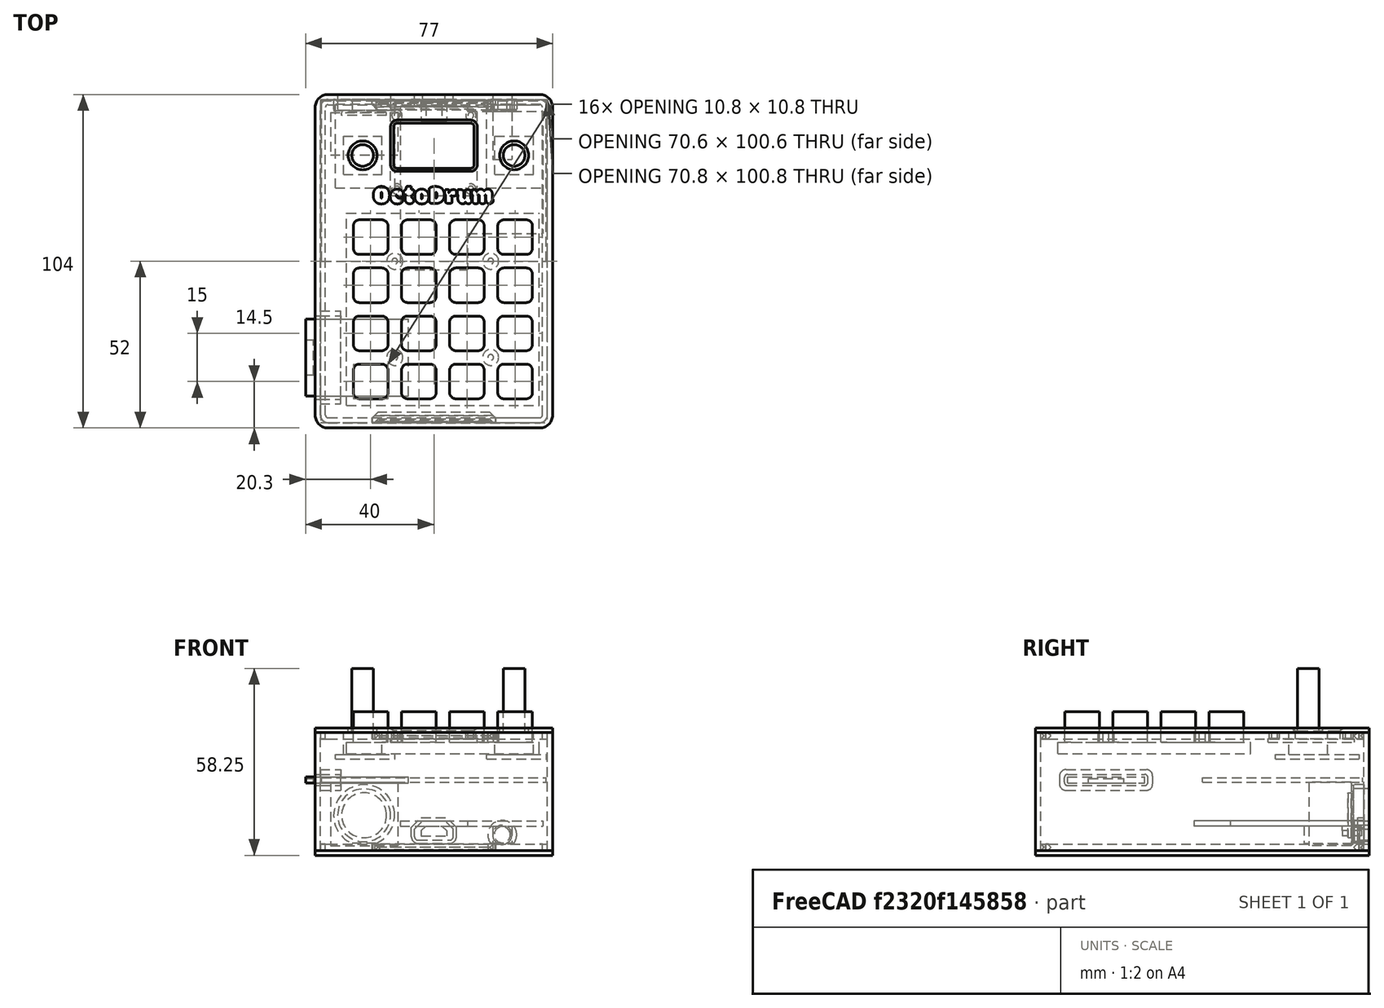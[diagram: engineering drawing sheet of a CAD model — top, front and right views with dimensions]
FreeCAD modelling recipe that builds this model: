
FCSTD DOCUMENT  (FreeCAD 0.19R14555 (Git shallow))
Label: rpi-pico-drum
License: All rights reserved
LicenseURL: http://en.wikipedia.org/wiki/All_rights_reserved
objects: Part::Box×36, Part::MultiFuse×26, Part::Fillet×24, Part::Cut×16, Part::FeaturePython×10, Part::Cylinder×9, Part::Chamfer×8, Part::MultiCommon×4, Mesh::Feature×2, Part::Part2DObjectPython×2, Part::Extrusion×2, Part::Feature×1
note: 138 computed .brp shape members not serialized (recipe doc carries the construction recipe); baked Part::Feature solids carry a one-line shape summary decoded from their .brp

FEATURE [Mesh::Feature] nt_top  label="nt-top"
  Placement = pos=(0,0,5) rot=(1,0,0;3.14159rad)
FEATURE [Part::Box] Box  label="BareFrontPlate"
  AttacherType = Attacher::AttachEngine3D
  Height = 1.5
  Length = 74
  Placement = pos=(-37,-37,3.5) rot=(0,0,1;0rad)
  Width = 104
FEATURE [Part::Box] Box001  label="NeoTrellisPCB"
  AttacherType = Attacher::AttachEngine3D
  Height = 1.5
  Length = 60
  Placement = pos=(-27.2,-30,0) rot=(0,0,1;0rad)
  Width = 60
FEATURE [Part::Box] Box002  label="Cube001"
  AttacherType = Attacher::AttachEngine3D
  Height = 9.5
  Length = 10.8
  Placement = pos=(2.1,2.1,0) rot=(0,0,1;0rad)
  Width = 10.8
FEATURE [Part::Fillet] Fillet  label="NeoTrellisButton"
  Base = -> Box002
  Edges = 4 edges r=1.9: [Edge1,Edge3,Edge5,Edge7]
  Placement = pos=(-30,0,0) rot=(0,0,1;0rad)
FEATURE [Part::Fillet] Fillet001  label="NeoTrellisButton001"
  Base = -> Box002
  Edges = 4 edges r=1.9: [Edge1,Edge3,Edge5,Edge7]
  Placement = pos=(-15,0,0) rot=(0,0,1;0rad)
FEATURE [Part::Fillet] Fillet002  label="NeoTrellisButton002"
  Base = -> Box002
  Edges = 4 edges r=1.9: [Edge1,Edge3,Edge5,Edge7]
FEATURE [Part::Fillet] Fillet003  label="NeoTrellisButton003"
  Base = -> Box002
  Edges = 4 edges r=1.9: [Edge1,Edge3,Edge5,Edge7]
  Placement = pos=(15,0,0) rot=(0,0,1;0rad)
FEATURE [Part::Fillet] Fillet004  label="NeoTrellisButton004"
  Base = -> Box002
  Edges = 4 edges r=1.9: [Edge1,Edge3,Edge5,Edge7]
  Placement = pos=(-30,15,0) rot=(0,0,1;0rad)
FEATURE [Part::Fillet] Fillet005  label="NeoTrellisButton005"
  Base = -> Box002
  Edges = 4 edges r=1.9: [Edge1,Edge3,Edge5,Edge7]
  Placement = pos=(15,15,0) rot=(0,0,1;0rad)
FEATURE [Part::Fillet] Fillet006  label="NeoTrellisButton006"
  Base = -> Box002
  Edges = 4 edges r=1.9: [Edge1,Edge3,Edge5,Edge7]
  Placement = pos=(-15,15,0) rot=(0,0,1;0rad)
FEATURE [Part::Fillet] Fillet007  label="NeoTrellisButton007"
  Base = -> Box002
  Edges = 4 edges r=1.9: [Edge1,Edge3,Edge5,Edge7]
  Placement = pos=(0,15,0) rot=(0,0,1;0rad)
FEATURE [Part::Fillet] Fillet008  label="NeoTrellisButton008"
  Base = -> Box002
  Edges = 4 edges r=1.9: [Edge1,Edge3,Edge5,Edge7]
  Placement = pos=(-30,-15,0) rot=(0,0,1;0rad)
FEATURE [Part::Fillet] Fillet009  label="NeoTrellisButton009"
  Base = -> Box002
  Edges = 4 edges r=1.9: [Edge1,Edge3,Edge5,Edge7]
  Placement = pos=(15,-15,0) rot=(0,0,1;0rad)
FEATURE [Part::Fillet] Fillet010  label="NeoTrellisButton010"
  Base = -> Box002
  Edges = 4 edges r=1.9: [Edge1,Edge3,Edge5,Edge7]
  Placement = pos=(-15,-15,0) rot=(0,0,1;0rad)
FEATURE [Part::Fillet] Fillet011  label="NeoTrellisButton011"
  Base = -> Box002
  Edges = 4 edges r=1.9: [Edge1,Edge3,Edge5,Edge7]
  Placement = pos=(0,-15,0) rot=(0,0,1;0rad)
FEATURE [Part::Fillet] Fillet012  label="NeoTrellisButton012"
  Base = -> Box002
  Edges = 4 edges r=1.9: [Edge1,Edge3,Edge5,Edge7]
  Placement = pos=(-30,-30,0) rot=(0,0,1;0rad)
FEATURE [Part::Fillet] Fillet013  label="NeoTrellisButton013"
  Base = -> Box002
  Edges = 4 edges r=1.9: [Edge1,Edge3,Edge5,Edge7]
  Placement = pos=(15,-30,0) rot=(0,0,1;0rad)
FEATURE [Part::Fillet] Fillet014  label="NeoTrellisButton014"
  Base = -> Box002
  Edges = 4 edges r=1.9: [Edge1,Edge3,Edge5,Edge7]
  Placement = pos=(-15,-30,0) rot=(0,0,1;0rad)
FEATURE [Part::Fillet] Fillet015  label="NeoTrellisButton015"
  Base = -> Box002
  Edges = 4 edges r=1.9: [Edge1,Edge3,Edge5,Edge7]
  Placement = pos=(0,-30,0) rot=(0,0,1;0rad)
FEATURE [Part::Box] Box003  label="BackbonePCB"
  AttacherType = Attacher::AttachEngine3D
  Height = 1.5
  Length = 70
  Placement = pos=(-35,15,-12) rot=(0,0,1;0rad)
  Width = 50
FEATURE [Part::Box] Box004  label="NeoTrellisButtonBase"
  AttacherType = Attacher::AttachEngine3D
  Height = 2
  Length = 60
  Placement = pos=(-30,-30,-2) rot=(0,0,1;0rad)
  Width = 60
FEATURE [Part::MultiFuse] Fusion  label="NeoTrellisButtons"
  Placement = pos=(2.8,0,3.5) rot=(0,0,1;0rad)
  Shapes = -> [Fillet,Fillet012,Fillet014,Fillet015,Fillet013,Fillet011,Fillet003,Fillet001,Fillet002,Fillet005,Fillet007,Fillet008,Fillet006,Fillet004,Fillet009,Fillet010,Box004]
FEATURE [Part::Box] Box005  label="DisplayPCB"
  AttacherType = Attacher::AttachEngine3D
  Height = 1.2
  Length = 27
  Placement = pos=(-13.5,35.5,0) rot=(0,0,1;0rad)
  Width = 27
FEATURE [Part::Box] Box008  label="Cube002"
  AttacherType = Attacher::AttachEngine3D
  Height = 6.75
  Length = 12
  Placement = pos=(-6,-6,1.5) rot=(0,0,1;0rad)
  Width = 12
FEATURE [Part::Cylinder] Cylinder
  Angle = 360
  AttacherType = Attacher::AttachEngine3D
  Height = 20
  Placement = pos=(0,0,8.25) rot=(0,0,1;0rad)
  Radius = 3.375
FEATURE [Part::Box] Box009  label="EncoderPCB003"
  AttacherType = Attacher::AttachEngine3D
  Height = 1.5
  Length = 18.63
  Placement = pos=(-8.5,-10.2,0) rot=(0,0,1;0rad)
  Width = 26.2
FEATURE [Part::MultiFuse] Fusion001  label="MenuEncoder"
  Placement = pos=(25,48,-4.75) rot=(0,0,1;0rad)
  Shapes = -> [Box008,Cylinder,Box009]
FEATURE [Part::MultiFuse] Fusion002  label="ModEncoder"
  Placement = pos=(-22.2,48,-4.75) rot=(0,0,1;0rad)
  Shapes = -> [Box008,Cylinder,Box009]
FEATURE [Part::MultiFuse] Fusion003  label="NeoTrellis"
  Placement = pos=(0,0,-3) rot=(0,0,1;0rad)
  Shapes = -> [Fusion,Box001]
FEATURE [Part::Box] Box010  label="Cube"
  AttacherType = Attacher::AttachEngine3D
  Height = 19.75
  Length = 21
  Placement = pos=(-10.5,0,0) rot=(0,0,1;0rad)
  Width = 13.25
FEATURE [Part::Cylinder] Cylinder001
  Angle = 360
  AttacherType = Attacher::AttachEngine3D
  Height = 1
  Placement = pos=(0,1,10.25) rot=(1,0,0;1.5708rad)
  Radius = 7
FEATURE [Part::Cut] Cut  label="MidiInput"
  Base = -> Box010
  Placement = pos=(-21.75,61.4,-12) rot=(1,0,0;3.14159rad)
  Tool = -> Cylinder001
FEATURE [Part::Box] Box011  label="PicoPCB"
  AttacherType = Attacher::AttachEngine3D
  Height = 1.6
  Length = 21
  Placement = pos=(-10.5,-25.5,0) rot=(0,0,1;0rad)
  Width = 51
FEATURE [Part::Box] Box012  label="Cube003"
  AttacherType = Attacher::AttachEngine3D
  Height = 3.1
  Length = 8
  Placement = pos=(-4,-26.8,1.6) rot=(0,0,1;0rad)
  Width = 6
FEATURE [Part::Chamfer] Chamfer  label="PicoUSB"
  Base = -> Box012
  Edges = 2 edges r=1.5: [Edge4,Edge8]
FEATURE [Part::MultiFuse] Fusion004  label="Pico"
  Placement = pos=(0,37.83,-24) rot=(1,0,0;3.14159rad)
  Shapes = -> [Chamfer,Box011]
FEATURE [Part::Box] Box013  label="I2SPCB"
  AttacherType = Attacher::AttachEngine3D
  Height = 1.6
  Length = 25.4
  Placement = pos=(-12.7,-19.05,0) rot=(0,0,1;0rad)
  Width = 38.1
FEATURE [Part::Box] Box014  label="Cube005"
  AttacherType = Attacher::AttachEngine3D
  Height = 5.5
  Length = 6
  Placement = pos=(-3,0,0) rot=(0,0,1;0rad)
  Width = 15
FEATURE [Part::Cylinder] Cylinder002
  Angle = 360
  AttacherType = Attacher::AttachEngine3D
  Height = 2.25
  Placement = pos=(0,0,2.75) rot=(1,0,0;1.5708rad)
  Radius = 2.5
FEATURE [Part::MultiFuse] Fusion005  label="AudioJack"
  Placement = pos=(0,-19,1.6) rot=(0,0,1;0rad)
  Shapes = -> [Cylinder002,Box014]
FEATURE [Part::MultiFuse] Fusion006  label="UDA1334A"
  Placement = pos=(21.3,42.7,-24) rot=(1,0,0;3.14159rad)
  Shapes = -> [Fusion005,Box013]
FEATURE [Part::Box] Box015  label="SDCard"
  AttacherType = Attacher::AttachEngine3D
  Height = 2
  Length = 32
  Placement = pos=(-16,-12,0) rot=(0,0,1;0rad)
  Width = 24
FEATURE [Part::Box] Box016  label="DisplayVisible"
  AttacherType = Attacher::AttachEngine3D
  Height = 1.8
  Length = 25
  Placement = pos=(-12.5,44,1.2) rot=(0,0,1;0rad)
  Width = 14
FEATURE [Part::MultiFuse] Fusion007  label="Display"
  Placement = pos=(0,0,0.5) rot=(0,0,1;0rad)
  Shapes = -> [Box005,Box016]
FEATURE [Part::Box] Box017  label="uSDCardSlot"
  AttacherType = Attacher::AttachEngine3D
  Height = 1.5
  Length = 2.5
  Placement = pos=(-16,-5.5,0) rot=(0,0,1;0rad)
  Width = 11
FEATURE [Part::Cut] Cut001  label="SDAdapter"
  Base = -> Box015
  Placement = pos=(-24,-15,-12.25) rot=(0,0,1;0rad)
  Tool = -> Box017
FEATURE [Part::MultiFuse] Fusion008  label="Internals"
  Shapes = -> [Box003,Cut,Cut001,Fusion003,Fusion007,Fusion001,Fusion004,Fusion006,Fusion002]
FEATURE [Part::MultiFuse] Fusion009  label="NeoTrellisButtons001"
  Placement = pos=(2.8,0,2.5) rot=(0,0,1;0rad)
  Shapes = -> [Fillet,Fillet012,Fillet014,Fillet015,Fillet013,Fillet011,Fillet003,Fillet001,Fillet002,Fillet005,Fillet007,Fillet008,Fillet006,Fillet004,Fillet009,Fillet010,Box004]
FEATURE [Part::Cylinder] Cylinder003
  Angle = 360
  AttacherType = Attacher::AttachEngine3D
  Height = 1.5
  Placement = pos=(-22.2,48,3.5) rot=(0,0,1;0rad)
  Radius = 4.5
FEATURE [Part::Cylinder] Cylinder004
  Angle = 360
  AttacherType = Attacher::AttachEngine3D
  Height = 1.5
  Placement = pos=(25,48,3.5) rot=(0,0,1;0rad)
  Radius = 4.5
FEATURE [Part::Box] Box018  label="Cube006"
  AttacherType = Attacher::AttachEngine3D
  Height = 1.5
  Length = 25
  Placement = pos=(-12.5,44,3.5) rot=(0,0,1;0rad)
  Width = 14
FEATURE [Part::MultiFuse] Fusion010  label="FrontPlateCutouts"
  Shapes = -> [Fusion009,Cylinder003,Cylinder004,Box018]
FEATURE [Part::Cut] Cut002
  Base = -> Box
  Tool = -> Fusion010
FEATURE [Part::Fillet] Fillet016
  Base = -> Cut002
  Edges = 8 edges: [Edge1 r=4,Edge3 r=4,Edge6 r=4,Edge145 r=4,Edge410 r=1,Edge411 r=1,Edge412 r=1,Edge413 r=1]
FEATURE [Part::Chamfer] Chamfer001
  Base = -> Fillet016
  Edges = 8 edges r=1: [Edge142,Edge143,Edge144,Edge145,Edge146,Edge147,Edge148,Edge149]
FEATURE [Part::Box] Box019  label="Cube007"
  AttacherType = Attacher::AttachEngine3D
  Height = 2
  Length = 1.5
  Placement = pos=(-35.3,-33,1.5) rot=(0,0,1;0rad)
  Width = 96
FEATURE [Part::Cylinder] Cylinder006
  Angle = 90
  AttacherType = Attacher::AttachEngine3D
  Height = 2
  Placement = pos=(33,33,1.5) rot=(0,0,1;0rad)
  Radius = 2.3
FEATURE [Part::Cylinder] Cylinder007
  Angle = 90
  AttacherType = Attacher::AttachEngine3D
  Height = 2
  Placement = pos=(33,33,1.5) rot=(0,0,1;0rad)
  Radius = 0.8
FEATURE [Part::Cut] Cut003  label="Corner"
  Base = -> Cylinder006
  Placement = pos=(0,30,0) rot=(0,0,1;0rad)
  Tool = -> Cylinder007
FEATURE [Part::Cut] Cut004  label="Corner001"
  Base = -> Cylinder006
  Placement = pos=(0,30,0) rot=(0,0,1;1.5708rad)
  Tool = -> Cylinder007
FEATURE [Part::Cut] Cut005  label="Corner002"
  Base = -> Cylinder006
  Placement = pos=(0,0,0) rot=(0,0,-1;1.5708rad)
  Tool = -> Cylinder007
FEATURE [Part::Cut] Cut006  label="Corner003"
  Base = -> Cylinder006
  Placement = pos=(0,0,0) rot=(0,0,1;3.14159rad)
  Tool = -> Cylinder007
FEATURE [Part::Box] Box020  label="Cube008"
  AttacherType = Attacher::AttachEngine3D
  Height = 2
  Length = 1.5
  Placement = pos=(33.8,-33,1.5) rot=(0,0,1;0rad)
  Width = 96
FEATURE [Part::Box] Box021  label="Cube009"
  AttacherType = Attacher::AttachEngine3D
  Height = 2
  Length = 66
  Placement = pos=(-33,-35.3,1.5) rot=(0,0,1;0rad)
  Width = 1.5
FEATURE [Part::Box] Box022  label="Cube010"
  AttacherType = Attacher::AttachEngine3D
  Height = 2
  Length = 66
  Placement = pos=(-33,63.8,1.5) rot=(0,0,1;0rad)
  Width = 1.5
FEATURE [Part::MultiFuse] Fusion011  label="FrontPlateFrame"
  Shapes = -> [Box022,Box020,Box021,Cut003,Cut004,Cut005,Cut006,Box019]
FEATURE [Part::MultiFuse] Fusion012  label="FrontPlate"
  Shapes = -> [Fusion011,Chamfer001]
FEATURE [Part::Box] Box023  label="BareBackPlate"
  AttacherType = Attacher::AttachEngine3D
  Height = 1.5
  Length = 74
  Placement = pos=(-37,-37,-34.75) rot=(0,0,1;0rad)
  Width = 104
FEATURE [Part::Fillet] Fillet017
  Base = -> Box023
  Edges = 4 edges r=4: [Edge1,Edge3,Edge5,Edge7]
FEATURE [Part::MultiFuse] Fusion013  label="FrontPlateFrame001"
  Placement = pos=(0,0,-34.75) rot=(0,0,1;0rad)
  Shapes = -> [Box022,Box020,Box021,Cut003,Cut004,Cut005,Cut006,Box019]
FEATURE [Part::MultiFuse] Fusion014  label="BottomPlate"
  Shapes = -> [Fillet017,Fusion013]
FEATURE [Part::FeaturePython] Tube  # WARN: FeaturePython — macro-defined, semantics opaque (R4)
  AttacherType = Attacher::AttachEngine3D
  Height = 3
  InnerRadius = 0.9
  OuterRadius = 2.5
  Placement = pos=(-12.2,-15,0.5) rot=(0,0,1;0rad)
FEATURE [Part::FeaturePython] Tube001  # WARN: FeaturePython — macro-defined, semantics opaque (R4)
  AttacherType = Attacher::AttachEngine3D
  Height = 3
  InnerRadius = 0.9
  OuterRadius = 2.5
  Placement = pos=(17.7,-15,0.5) rot=(0,0,1;0rad)
FEATURE [Part::FeaturePython] Tube002  # WARN: FeaturePython — macro-defined, semantics opaque (R4)
  AttacherType = Attacher::AttachEngine3D
  Height = 3
  InnerRadius = 0.9
  OuterRadius = 2.5
  Placement = pos=(-12.2,15,0.5) rot=(0,0,1;0rad)
FEATURE [Part::FeaturePython] Tube003  # WARN: FeaturePython — macro-defined, semantics opaque (R4)
  AttacherType = Attacher::AttachEngine3D
  Height = 3
  InnerRadius = 0.9
  OuterRadius = 2.5
  Placement = pos=(17.7,15,0.5) rot=(0,0,1;0rad)
FEATURE [Part::FeaturePython] Tube004  # WARN: FeaturePython — macro-defined, semantics opaque (R4)
  AttacherType = Attacher::AttachEngine3D
  Height = 1.8
  InnerRadius = 0.9
  OuterRadius = 1.6
  Placement = pos=(-11.5,60.5,1.7) rot=(0,0,1;0rad)
FEATURE [Part::FeaturePython] Tube005  # WARN: FeaturePython — macro-defined, semantics opaque (R4)
  AttacherType = Attacher::AttachEngine3D
  Height = 1.8
  InnerRadius = 0.9
  OuterRadius = 1.6
  Placement = pos=(11.5,60.5,1.7) rot=(0,0,1;0rad)
FEATURE [Part::FeaturePython] Tube006  # WARN: FeaturePython — macro-defined, semantics opaque (R4)
  AttacherType = Attacher::AttachEngine3D
  Height = 1.8
  InnerRadius = 0.9
  OuterRadius = 1.6
  Placement = pos=(-11.5,37.5,1.7) rot=(0,0,1;0rad)
FEATURE [Part::FeaturePython] Tube007  # WARN: FeaturePython — macro-defined, semantics opaque (R4)
  AttacherType = Attacher::AttachEngine3D
  Height = 1.8
  InnerRadius = 0.9
  OuterRadius = 1.6
  Placement = pos=(11.5,37.5,1.7) rot=(0,0,1;0rad)
FEATURE [Part::MultiFuse] Fusion015  label="NeoTrellisMounts"
  Shapes = -> [Tube,Tube001,Tube002,Tube003]
FEATURE [Part::MultiFuse] Fusion016  label="DisplayMounts"
  Shapes = -> [Tube004,Tube005,Tube006,Tube007]
FEATURE [Part::MultiFuse] Fusion017
  Shapes = -> [Fusion016,Fusion015,Fusion012]
FEATURE [Part::Part2DObjectPython] ShapeString001  # Draft 2D object (typed FeaturePython)
  FontFile = <userpath>/repos/dcdalrymple/tools/octodrum/assets/Modak-Regular.ttf
  Placement = pos=(-19,33,4.8) rot=(0,0,1;0rad)
  Size = 8
  String = OctoDr
  Tracking = 0
FEATURE [Part::Part2DObjectPython] ShapeString002  # Draft 2D object (typed FeaturePython)
  FontFile = <userpath>/repos/dcdalrymple/tools/octodrum/assets/Modak-Regular.ttf
  Placement = pos=(7.3,33,4.8) rot=(0,0,1;0rad)
  Size = 8
  String = um
  Tracking = 0
FEATURE [Part::Extrusion] Extrude
  Base = -> ShapeString001
  Dir = (0,0,1)
  DirMode = 0
  FaceMakerClass = Part::FaceMakerBullseye
  LengthFwd = 0.4
  LengthRev = 0
  Solid = false
  Symmetric = false
FEATURE [Part::Extrusion] Extrude001
  Base = -> ShapeString002
  Dir = (0,0,1)
  DirMode = 0
  FaceMakerClass = Part::FaceMakerBullseye
  LengthFwd = 0.4
  LengthRev = 0
  Solid = false
  Symmetric = false
FEATURE [Part::MultiFuse] Fusion018  label="Logo"
  Shapes = -> [Extrude,Extrude001]
FEATURE [Part::Cut] Cut007  label="FinalTopPlate"
  Base = -> Fusion017
  Tool = -> Fusion018
FEATURE [Part::Box] Box024  label="Cube011"
  AttacherType = Attacher::AttachEngine3D
  Height = 2
  Length = 38.5
  Placement = pos=(-19.25,-35.3,1.49) rot=(0,0,1;0rad)
  Width = 3.25
FEATURE [Part::Feature] nt_top001_solid  label="nt_top001 (Solid)"
  shape: bbox 74 x 74 x 3.5 mm, 2332 faces (baked)
FEATURE [Part::MultiCommon] Common  label="Snap"
  Placement = pos=(0,0,-34.75) rot=(0,0,1;0rad)
  Shapes = -> [nt_top001_solid,Box024]
FEATURE [Part::Box] Box025  label="Cube012"
  AttacherType = Attacher::AttachEngine3D
  Height = 2
  Length = 38.5
  Placement = pos=(-19.25,-35.3,-33.24) rot=(0,0,1;0rad)
  Width = 100.6
FEATURE [Part::MultiCommon] Common001  label="Snap001"
  Placement = pos=(0,30,-34.75) rot=(0,0,1;3.14159rad)
  Shapes = -> [nt_top001_solid,Box024]
FEATURE [Part::MultiCommon] Common002  label="Snap002"
  Placement = pos=(0,30,0) rot=(0,0,1;3.14159rad)
  Shapes = -> [nt_top001_solid,Box024]
FEATURE [Part::MultiCommon] Common003  label="Snap003"
  Shapes = -> [nt_top001_solid,Box024]
FEATURE [Part::Cut] Cut008
  Base = -> Fusion014
  Tool = -> Box025
FEATURE [Part::MultiFuse] Fusion019  label="BottomPlateSnap"
  Shapes = -> [Common,Common001,Cut008]
FEATURE [Part::Box] Box026  label="Cube013"
  AttacherType = Attacher::AttachEngine3D
  Height = 2
  Length = 38.5
  Placement = pos=(-19.25,-35.3,1.49) rot=(0,0,1;0rad)
  Width = 1.5
FEATURE [Part::Box] Box027  label="Cube014"
  AttacherType = Attacher::AttachEngine3D
  Height = 2
  Length = 38.5
  Placement = pos=(-19.25,63.8,1.49) rot=(0,0,1;0rad)
  Width = 1.5
FEATURE [Part::MultiFuse] Fusion020
  Shapes = -> [Box026,Box027]
FEATURE [Part::Cut] Cut009
  Base = -> Cut007
  Tool = -> Fusion020
FEATURE [Part::MultiFuse] Fusion021  label="TopPlateSnap"
  Shapes = -> [Common003,Common002,Cut009]
FEATURE [Part::Box] Box028  label="Cube015"
  AttacherType = Attacher::AttachEngine3D
  Height = 1.8
  Length = 34
  Placement = pos=(-17,39,32) rot=(0,0,1;0rad)
  Width = 0.9
FEATURE [Part::Chamfer] Chamfer002  label="SnapEdge"
  Base = -> Box028
  Edges = 2 edges r=0.89: [Edge9,Edge10]
  Placement = pos=(0,25.4,-30.4) rot=(0,0,1;0rad)
FEATURE [Mesh::Feature] frame
  Placement = pos=(5,5,0) rot=(0,0,1;0rad)
FEATURE [Part::Box] Box029  label="BareBackPlate001"
  AttacherType = Attacher::AttachEngine3D
  Height = 36.75
  Length = 74
  Placement = pos=(-37,-37,-33.25) rot=(0,0,1;0rad)
  Width = 104
FEATURE [Part::Box] Box030  label="BareBackPlate002"
  AttacherType = Attacher::AttachEngine3D
  Height = 36.75
  Length = 70.8
  Placement = pos=(-35.4,-35.4,-33.25) rot=(0,0,1;0rad)
  Width = 100.8
FEATURE [Part::Fillet] Fillet018
  Base = -> Box030
  Edges = 4 edges r=2.4: [Edge1,Edge3,Edge5,Edge7]
FEATURE [Part::Fillet] Fillet019
  Base = -> Box029
  Edges = 4 edges r=4: [Edge1,Edge3,Edge5,Edge7]
FEATURE [Part::Cut] Cut010  label="EmptyFrame"
  Base = -> Fillet019
  Tool = -> Fillet018
FEATURE [Part::Chamfer] Chamfer003  label="SnapEdge001"
  Base = -> Box028
  Edges = 2 edges r=0.89: [Edge9,Edge10]
  Placement = pos=(0,4.6,-30.4) rot=(0,0,1;3.14159rad)
FEATURE [Part::Chamfer] Chamfer004  label="SnapEdge002"
  Base = -> Box028
  Edges = 2 edges r=0.89: [Edge9,Edge10]
  Placement = pos=(0,25.4,-65.15) rot=(0,0,1;0rad)
FEATURE [Part::Chamfer] Chamfer005  label="SnapEdge003"
  Base = -> Box028
  Edges = 2 edges r=0.89: [Edge9,Edge10]
  Placement = pos=(0,4.6,-65.15) rot=(0,0,1;3.14159rad)
FEATURE [Part::MultiFuse] Fusion022  label="EmptyFrameSnap"
  Shapes = -> [Chamfer002,Chamfer003,Chamfer005,Chamfer004,Cut010]
FEATURE [Part::Cylinder] Cylinder008
  Angle = 360
  AttacherType = Attacher::AttachEngine3D
  Height = 4
  Placement = pos=(21.3,67,-28.35) rot=(1,0,0;1.5708rad)
  Radius = 3
FEATURE [Part::FeaturePython] Tube008  # WARN: FeaturePython — macro-defined, semantics opaque (R4)
  AttacherType = Attacher::AttachEngine3D
  Height = 4.75
  InnerRadius = 3
  OuterRadius = 4.5
  Placement = pos=(21.3,67,-28.35) rot=(1,0,0;1.5708rad)
FEATURE [Part::FeaturePython] Tube009  # WARN: FeaturePython — macro-defined, semantics opaque (R4)
  AttacherType = Attacher::AttachEngine3D
  Height = 5
  InnerRadius = 8.25
  OuterRadius = 9.5
  Placement = pos=(-21.75,67,-22.25) rot=(1,0,0;1.5708rad)
FEATURE [Part::Cylinder] Cylinder009
  Angle = 360
  AttacherType = Attacher::AttachEngine3D
  Height = 5
  Placement = pos=(-21.75,67,-22.25) rot=(1,0,0;1.5708rad)
  Radius = 8.25
FEATURE [Part::Box] Box031  label="Cube016"
  AttacherType = Attacher::AttachEngine3D
  Height = 6
  Length = 12
  Placement = pos=(-6,63.5,-30) rot=(0,0,1;0rad)
  Width = 3.5
FEATURE [Part::Chamfer] Chamfer006
  Base = -> Box031
  Edges = 2 edges r=2.5: [Edge2,Edge6]
FEATURE [Part::Box] Box032  label="Cube017"
  AttacherType = Attacher::AttachEngine3D
  Height = 8
  Length = 14
  Placement = pos=(-7,63.5,-31) rot=(0,0,1;0rad)
  Width = 3.5
FEATURE [Part::Chamfer] Chamfer008
  Base = -> Box032
  Edges = 2 edges r=3: [Edge2,Edge6]
FEATURE [Part::Fillet] Fillet020
  Base = -> Chamfer006
  Edges = 2 edges r=1: [Edge2,Edge13]
FEATURE [Part::Fillet] Fillet021
  Base = -> Chamfer008
  Edges = 2 edges r=2: [Edge2,Edge13]
FEATURE [Part::Fillet] Fillet022
  Base = -> Chamfer006
  Edges = 2 edges r=1: [Edge2,Edge13]
FEATURE [Part::Cut] Cut011
  Base = -> Fillet021
  Tool = -> Fillet020
FEATURE [Part::Box] Box033  label="Cube018"
  AttacherType = Attacher::AttachEngine3D
  Height = 2
  Length = 9
  Placement = pos=(16.8,62.25,-33) rot=(0,0,1;0rad)
  Width = 4.75
FEATURE [Part::Cut] Cut013
  Base = -> Tube008
  Tool = -> Box033
FEATURE [Part::Box] Box034  label="Cube019"
  AttacherType = Attacher::AttachEngine3D
  Height = 2
  Length = 19
  Placement = pos=(-31.2,62,-33) rot=(0,0,1;0rad)
  Width = 5
FEATURE [Part::Cut] Cut014
  Base = -> Tube009
  Tool = -> Box034
FEATURE [Part::Box] Box035  label="Cube020"
  AttacherType = Attacher::AttachEngine3D
  Height = 3.5
  Length = 8
  Placement = pos=(-37,-28,-13) rot=(0,0,1;0rad)
  Width = 26
FEATURE [Part::Box] Box036  label="Cube021"
  AttacherType = Attacher::AttachEngine3D
  Height = 6.5
  Length = 8
  Placement = pos=(-37,-29.5,-14.5) rot=(0,0,1;0rad)
  Width = 29
FEATURE [Part::Box] Box037  label="Cube022"
  AttacherType = Attacher::AttachEngine3D
  Height = 3.5
  Length = 8
  Placement = pos=(-37,-28,-13) rot=(0,0,1;0rad)
  Width = 26
FEATURE [Part::Cut] Cut015
  Base = -> Box036
  Tool = -> Box035
FEATURE [Part::MultiFuse] Fusion025  label="PortCuts"
  Shapes = -> [Cylinder008,Fillet022,Cylinder009,Box037]
FEATURE [Part::Fillet] Fillet023
  Base = -> Cut015
  Edges = 8 edges: [Edge9 r=2,Edge11 r=2,Edge12 r=2,Edge14 r=2,Edge17 r=1,Edge19 r=1,Edge20 r=1,Edge23 r=1]
FEATURE [Part::MultiFuse] Fusion026  label="PortGuides"
  Shapes = -> [Cut011,Cut013,Cut014,Fillet023]
FEATURE [Part::Cut] Cut016
  Base = -> Fusion022
  Tool = -> Fusion025
FEATURE [Part::MultiFuse] Fusion027  label="FrameSnap"
  Shapes = -> [Fusion026,Cut016]
